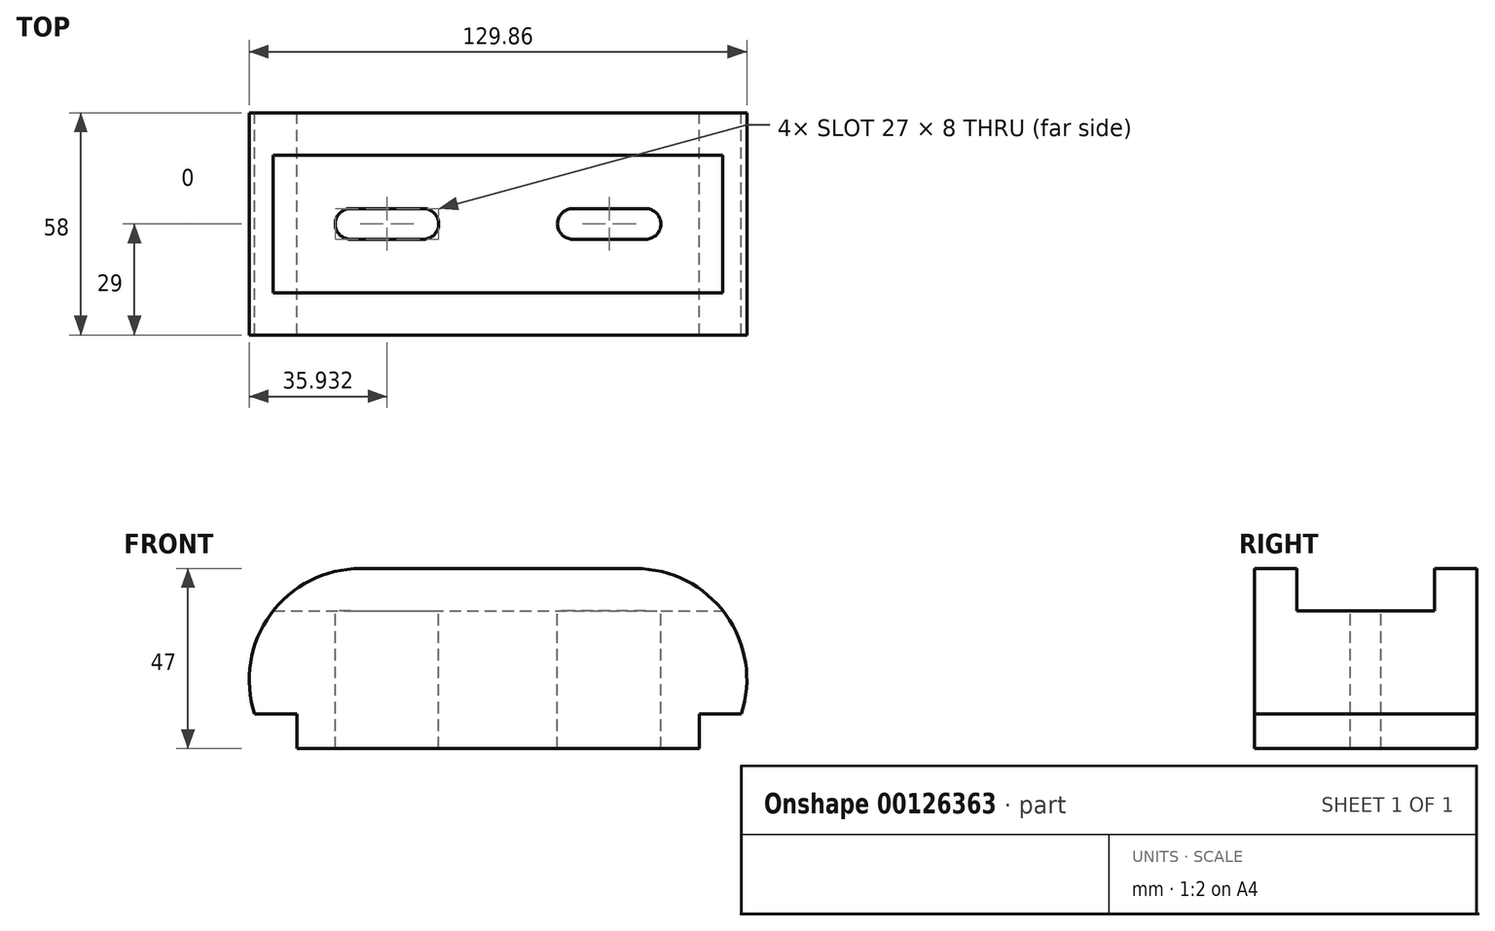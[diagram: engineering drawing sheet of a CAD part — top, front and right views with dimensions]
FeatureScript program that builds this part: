
annotation { "Feature Type Name" : "Feature", "Feature Type Description" : "" }
export const myFeature = defineFeature(function(context is Context, id is Id, definition is map)
    precondition{}
    {
        {
            var Q0;
            Q0=qCreatedBy(makeId("Front.planeOp"),FACE);
            var sketch = newSketch(context, id + "F0", { "sketchPlane" : qUnion([Q0])});
            skLineSegment(sketch, "E0", {"start": v(-51.5, 0) * mm, "end": v(53.5, 0) * mm});
            skLineSegment(sketch, "E1", {"start": v(-51.5, 0) * mm, "end": v(-51.5, 9) * mm});
            skLineSegment(sketch, "E2", {"start": v(53.5, 0) * mm, "end": v(53.5, 9) * mm});
            skLineSegment(sketch, "E3", {"start": v(-51.5, 9) * mm, "end": v(-62.5, 9) * mm});
            skLineSegment(sketch, "E4", {"start": v(53.5, 9) * mm, "end": v(64.5, 9) * mm});
            skArc(sketch, "E5", {"start": v(-34.93, 47) * mm, "mid": v(-58.4, 35.03) * mm, "end": v(-62.5, 9) * mm});
            skArc(sketch, "E6", {"start": v(64.5, 9) * mm, "mid": v(60.4, 35.03) * mm, "end": v(36.93, 47) * mm});
            skLineSegment(sketch, "E7", {"start": v(-34.93, 47) * mm, "end": v(36.93, 47) * mm});
            skSolve(sketch);
        }
        {
            var Q0;
            Q0 = qSketchRegion(id + "F0", true);
            extrude(context, id + "F1", {"entities" : qUnion([Q0]), "endBound" : BoundingType.SYMMETRIC, "depth" : 58 * mm});
        }
        {
            var Q0;
            Q0=qCreatedBy(makeId("Right.planeOp"),FACE);
            var sketch = newSketch(context, id + "F2", { "sketchPlane" : qUnion([Q0])});
            skLineSegment(sketch, "E8", {"start": v(-29, 36) * mm, "end": v(0, 36) * mm, "construction": true});
            skLineSegment(sketch, "E9.bottom", {"start": v(-18, 36) * mm, "end": v(18, 36) * mm});
            skLineSegment(sketch, "E9.top", {"start": v(-18, 47) * mm, "end": v(18, 47) * mm});
            skLineSegment(sketch, "E9.left", {"start": v(-18, 36) * mm, "end": v(-18, 47) * mm});
            skLineSegment(sketch, "E9.right", {"start": v(18, 36) * mm, "end": v(18, 47) * mm});
            skSolve(sketch);
        }
        {
            var Q0;
            Q0 = qSketchRegion(id + "F2", true);
            extrude(context, id + "F3", {"entities" : qUnion([Q0]), "operationType" : NewBodyOperationType.REMOVE, "endBound" : BoundingType.SYMMETRIC, "oppositeDirection" : true, "depth" : 127 * mm});
        }
        {
            var Q0;
            Q0=qCreatedBy(makeId("Top.planeOp"),FACE);
            var sketch = newSketch(context, id + "F4", { "sketchPlane" : qUnion([Q0])});
            skArc(sketch, "E10", {"start": v(-37.5, 4) * mm, "mid": v(-41.5, 0) * mm, "end": v(-37.5, -4) * mm});
            skArc(sketch, "E11", {"start": v(-18.5, -4) * mm, "mid": v(-14.5, 0) * mm, "end": v(-18.5, 4) * mm});
            skLineSegment(sketch, "E12", {"start": v(-51.5, 0) * mm, "end": v(53.5, 0) * mm, "construction": true});
            skPoint(sketch, "E12.endSnap0", {"position": v(-14.5, 0) * mm});
            skLineSegment(sketch, "E13", {"start": v(-18.5, 4) * mm, "end": v(-37.5, 4) * mm});
            skLineSegment(sketch, "E14", {"start": v(-37.5, -4) * mm, "end": v(-18.5, -4) * mm});
            skArc(sketch, "E15", {"start": v(39.5, -4) * mm, "mid": v(43.5, 0) * mm, "end": v(39.5, 4) * mm});
            skArc(sketch, "E16", {"start": v(20.5, 4) * mm, "mid": v(16.5, 0) * mm, "end": v(20.5, -4) * mm});
            skLineSegment(sketch, "E17", {"start": v(20.5, 4) * mm, "end": v(39.5, 4) * mm});
            skLineSegment(sketch, "E18", {"start": v(20.5, -4) * mm, "end": v(39.5, -4) * mm});
            skSolve(sketch);
        }
        {
            var Q0;
            Q0 = qSketchRegion(id + "F4", true);
            extrude(context, id + "F5", {"entities" : qUnion([Q0]), "operationType" : NewBodyOperationType.REMOVE, "endBound" : BoundingType.SYMMETRIC, "oppositeDirection" : true, "depth" : 100 * mm});
        }
    });
